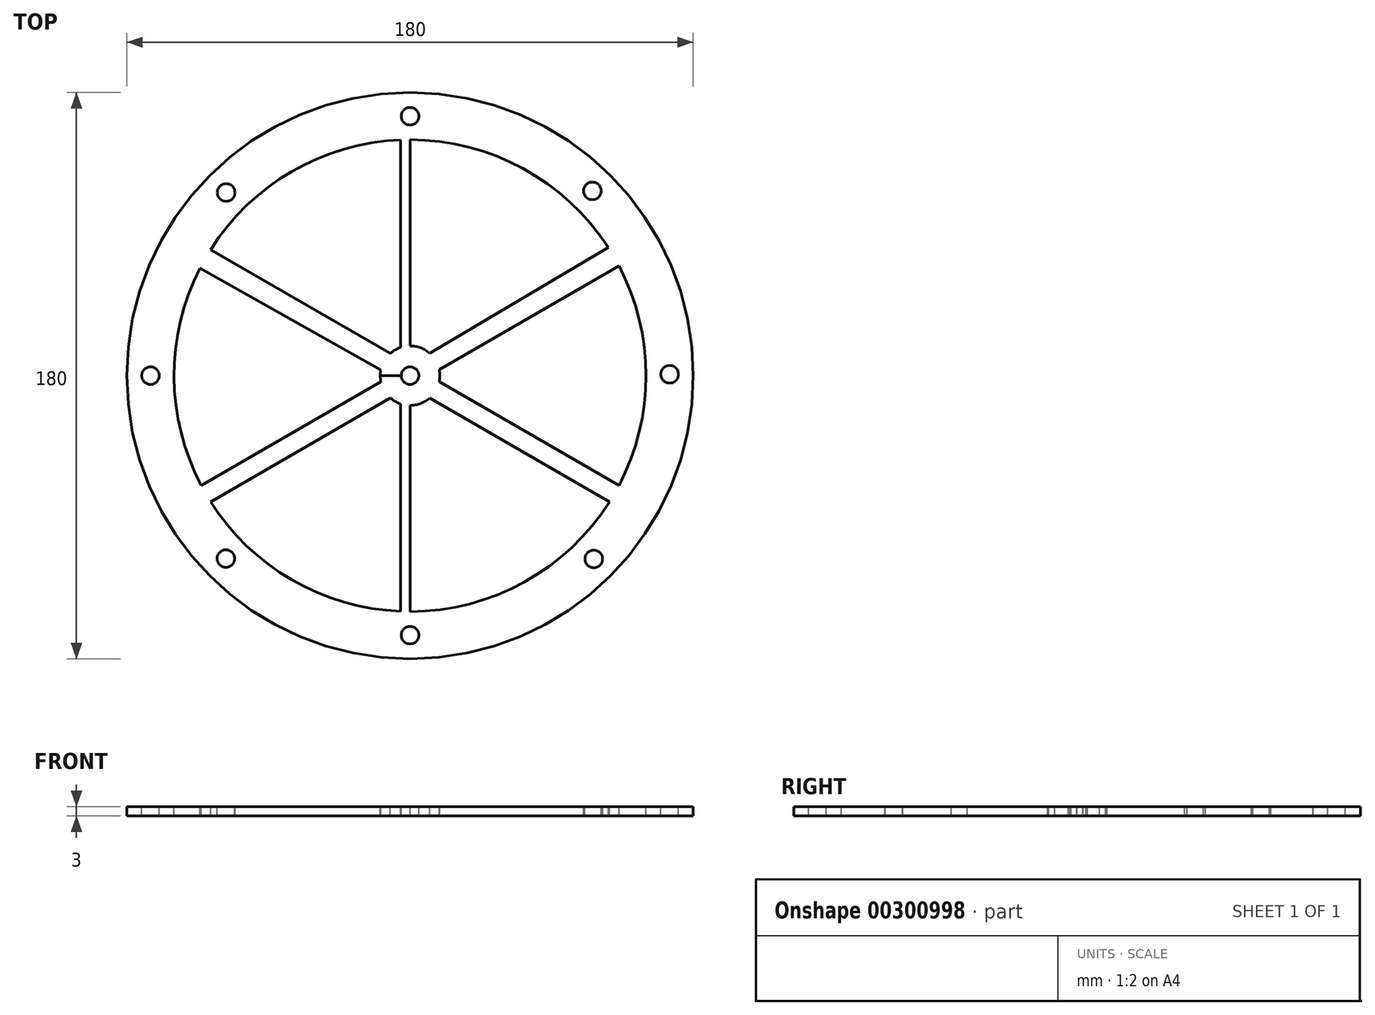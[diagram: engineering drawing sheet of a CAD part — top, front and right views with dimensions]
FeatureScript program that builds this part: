
annotation { "Feature Type Name" : "Feature", "Feature Type Description" : "" }
export const myFeature = defineFeature(function(context is Context, id is Id, definition is map)
    precondition{}
    {
        {
            var Q0;
            Q0=qCreatedBy(makeId("Top.planeOp"),FACE);
            var sketch = newSketch(context, id + "F0", { "sketchPlane" : qUnion([Q0])});
            skCircle(sketch, "E0", {"center": v(0, 0) * mm, "radius": 90 * mm});
            skCircle(sketch, "E1", {"center": v(0, 0) * mm, "radius": 75 * mm});
            skPoint(sketch, "E2", {"position": v(0, 82.48) * mm});
            skPoint(sketch, "E3", {"position": v(0, -82.5) * mm});
            skPoint(sketch, "E4", {"position": v(-75, 0) * mm});
            skPoint(sketch, "E5", {"position": v(-82.5, 0) * mm});
            skPoint(sketch, "E6", {"position": v(-58.44, 58.23) * mm});
            skPoint(sketch, "E7", {"position": v(82.5, 0.44) * mm});
            skPoint(sketch, "E8", {"position": v(57.94, 58.73) * mm});
            skPoint(sketch, "E9", {"position": v(-58.53, -58.15) * mm});
            skLineSegment(sketch, "E10", {"start": v(0, 0) * mm, "end": v(0, 0) * mm});
            skPoint(sketch, "E11", {"position": v(58.39, -58.28) * mm});
            skLineSegment(sketch, "E12", {"start": v(3, 74.94) * mm, "end": v(3, 8.6) * mm});
            skLineSegment(sketch, "E13", {"start": v(0, 75) * mm, "end": v(0, 0) * mm, "construction": true});
            skLineSegment(sketch, "E14", {"start": v(0, 75) * mm, "end": v(0, -75) * mm});
            skCircle(sketch, "E15", {"center": v(0, 0) * mm, "radius": 9.46 * mm});
            skLineSegment(sketch, "E16", {"start": v(0, 0) * mm, "end": v(82.5, 0.44) * mm});
            skLineSegment(sketch, "E17", {"start": v(-3, -8.98) * mm, "end": v(-3, -74.94) * mm});
            skLineSegment(sketch, "E18", {"start": v(0, 0) * mm, "end": v(-75, 0) * mm});
            skLineSegment(sketch, "E19", {"start": v(3, -74.88) * mm, "end": v(0, -75) * mm});
            skLineSegment(sketch, "E20", {"start": v(-3, 74.94) * mm, "end": v(-3, 8.97) * mm});
            skLineSegment(sketch, "E21.MirrorCS", {"start": v(0, 0) * mm, "end": v(-75, -0.8) * mm});
            skLineSegment(sketch, "E22.MirrorCS", {"start": v(3.8, -74.9) * mm, "end": v(3.1, -8.57) * mm});
            skLineSegment(sketch, "E23.1.0", {"start": v(62.97, 40.75) * mm, "end": v(5.88, 6.96) * mm});
            skLineSegment(sketch, "E23.2.0", {"start": v(-66.77, 34.16) * mm, "end": v(-8.97, 1.6) * mm});
            skLineSegment(sketch, "E24.1.0", {"start": v(9.27, 1.9) * mm, "end": v(66.4, 34.87) * mm});
            skLineSegment(sketch, "E24.1.1", {"start": v(-66.4, -34.87) * mm, "end": v(-8.95, -1.7) * mm});
            skLineSegment(sketch, "E24.2.0", {"start": v(-6.27, 7.09) * mm, "end": v(-63.4, 40.07) * mm});
            skLineSegment(sketch, "E24.2.1", {"start": v(63.4, -40.07) * mm, "end": v(5.95, -6.9) * mm});
            skLineSegment(sketch, "E25.1.0", {"start": v(-63.4, -40.07) * mm, "end": v(-6.27, -7.08) * mm});
            skLineSegment(sketch, "E25.2.0", {"start": v(66.4, -34.87) * mm, "end": v(9.27, -1.89) * mm});
            skCircle(sketch, "E26", {"center": v(0, 0) * mm, "radius": 2.8 * mm});
            skSolve(sketch);
        }
        {
            var Q0;
            Q0=makeQuery(id+"F0.imprint","IMPRINT",FACE,{"disambiguationData":[TD([[makeQuery(id+"F0.imprint","IMPRINT",EDGE,{"derivedFrom":sQuery(id+"F0.wireOp",EDGE,"E0")}),1.0]])]});
            var Q1;
            {var subQ1=sQuery(id+"F0.wireOp",EDGE,"E1");var subQ3=sQuery(id+"F0.wireOp",EDGE,"E14");var subQ4=makeQuery(id+"F0.imprint","INTERSECT",VERTEX,{"disambiguationData":[OD(0.0)],"derivedFrom":[subQ1,subQ3]});Q1=makeQuery(id+"F0.imprint","IMPRINT",FACE,{"disambiguationData":[TD([[makeQuery(id+"F0.imprint","IMPRINT",EDGE,{"disambiguationData":[TD([[subQ4,-1.0]])],"derivedFrom":subQ3}),1.0]])]});}
            var Q2;
            {var subQ0=sQuery(id+"F0.wireOp",EDGE,"E14");var subQ1=sQuery(id+"F0.wireOp",EDGE,"E1");var subQ2=makeQuery(id+"F0.imprint","INTERSECT",VERTEX,{"disambiguationData":[OD(0.0)],"derivedFrom":[subQ1,subQ0]});Q2=makeQuery(id+"F0.imprint","IMPRINT",FACE,{"disambiguationData":[TD([[makeQuery(id+"F0.imprint","IMPRINT",EDGE,{"disambiguationData":[TD([[subQ2,-1.0]])],"derivedFrom":subQ0}),-1.0]])]});}
            var Q3;
            {var subQ7=sQuery(id+"F0.wireOp",EDGE,"E24.2.0");Q3=makeQuery(id+"F0.imprint","IMPRINT",FACE,{"disambiguationData":[TD([[makeQuery(id+"F0.imprint","IMPRINT",EDGE,{"derivedFrom":subQ7}),1.0]])]});}
            var Q4;
            {var subQ3=sQuery(id+"F0.wireOp",EDGE,"E24.1.0");Q4=makeQuery(id+"F0.imprint","IMPRINT",FACE,{"disambiguationData":[TD([[makeQuery(id+"F0.imprint","IMPRINT",EDGE,{"derivedFrom":subQ3}),1.0]])]});}
            var Q5;
            {var subQ0=sQuery(id+"F0.wireOp",EDGE,"E24.2.1");var subQ1=sQuery(id+"F0.wireOp",EDGE,"E1");var subQ2=makeQuery(id+"F0.imprint","INTERSECT",VERTEX,{"derivedFrom":[subQ1,subQ0]});Q5=makeQuery(id+"F0.imprint","IMPRINT",FACE,{"disambiguationData":[TD([[makeQuery(id+"F0.imprint","IMPRINT",EDGE,{"disambiguationData":[TD([[subQ2,-1.0]])],"derivedFrom":subQ1}),1.0]])]});}
            var Q6;
            {var subQ3=sQuery(id+"F0.wireOp",EDGE,"E17");Q6=makeQuery(id+"F0.imprint","IMPRINT",FACE,{"disambiguationData":[TD([[makeQuery(id+"F0.imprint","IMPRINT",EDGE,{"derivedFrom":subQ3}),1.0]])]});}
            var Q7;
            {var subQ0=sQuery(id+"F0.wireOp",EDGE,"E14");var subQ1=sQuery(id+"F0.wireOp",EDGE,"E1");var subQ2=makeQuery(id+"F0.imprint","INTERSECT",VERTEX,{"disambiguationData":[OD(1.0)],"derivedFrom":[subQ1,subQ0]});Q7=makeQuery(id+"F0.imprint","IMPRINT",FACE,{"disambiguationData":[TD([[makeQuery(id+"F0.imprint","IMPRINT",EDGE,{"disambiguationData":[TD([[subQ2,-1.0]])],"derivedFrom":subQ1}),1.0]])]});}
            var Q8;
            {var subQ0=sQuery(id+"F0.wireOp",EDGE,"E24.1.1");var subQ1=sQuery(id+"F0.wireOp",EDGE,"E1");var subQ2=makeQuery(id+"F0.imprint","INTERSECT",VERTEX,{"derivedFrom":[subQ1,subQ0]});Q8=makeQuery(id+"F0.imprint","IMPRINT",FACE,{"disambiguationData":[TD([[makeQuery(id+"F0.imprint","IMPRINT",EDGE,{"disambiguationData":[TD([[subQ2,-1.0]])],"derivedFrom":subQ1}),1.0]])]});}
            var Q9;
            {var subQ0=sQuery(id+"F0.wireOp",EDGE,"E15");var subQ3=makeQuery(id+"F0.imprint","INTERSECT",VERTEX,{"derivedFrom":[subQ0,sQuery(id+"F0.wireOp",EDGE,"E24.1.1")]});Q9=makeQuery(id+"F0.imprint","IMPRINT",FACE,{"disambiguationData":[TD([[makeQuery(id+"F0.imprint","IMPRINT",EDGE,{"disambiguationData":[TD([[subQ3,1.0]])],"derivedFrom":subQ0}),1.0]])]});}
            var Q10;
            {var subQ0=sQuery(id+"F0.wireOp",EDGE,"E15");var subQ3=makeQuery(id+"F0.imprint","INTERSECT",VERTEX,{"derivedFrom":[subQ0,sQuery(id+"F0.wireOp",EDGE,"E20")]});Q10=makeQuery(id+"F0.imprint","IMPRINT",FACE,{"disambiguationData":[TD([[makeQuery(id+"F0.imprint","IMPRINT",EDGE,{"disambiguationData":[TD([[subQ3,1.0]])],"derivedFrom":subQ0}),1.0]])]});}
            var Q11;
            {var subQ0=sQuery(id+"F0.wireOp",EDGE,"E15");var subQ1=makeQuery(id+"F0.imprint","INTERSECT",VERTEX,{"derivedFrom":[subQ0,sQuery(id+"F0.wireOp",EDGE,"E24.1.0")]});Q11=makeQuery(id+"F0.imprint","IMPRINT",FACE,{"disambiguationData":[TD([[makeQuery(id+"F0.imprint","IMPRINT",EDGE,{"disambiguationData":[TD([[subQ1,1.0]])],"derivedFrom":subQ0}),1.0]])]});}
            var Q12;
            {var subQ0=sQuery(id+"F0.wireOp",EDGE,"E15");var subQ3=makeQuery(id+"F0.imprint","INTERSECT",VERTEX,{"derivedFrom":[subQ0,sQuery(id+"F0.wireOp",EDGE,"E22.MirrorCS")]});Q12=makeQuery(id+"F0.imprint","IMPRINT",FACE,{"disambiguationData":[TD([[makeQuery(id+"F0.imprint","IMPRINT",EDGE,{"disambiguationData":[TD([[subQ3,1.0]])],"derivedFrom":subQ0}),1.0]])]});}
            extrude(context, id + "F1", {"entities" : qUnion([Q0, Q1, Q2, Q3, Q4, Q5, Q6, Q7, Q8, Q9, Q10, Q11, Q12]), "oppositeDirection" : true, "offsetDistance" : 25 * mm, "depth" : 3 * mm});
        }
        {
            var Q0;
            Q0=sQuery(id+"F0.wireOp",VERTEX,"E5");
            var Q1;
            Q1=sQuery(id+"F0.wireOp",VERTEX,"E2");
            var Q2;
            Q2=sQuery(id+"F0.wireOp",VERTEX,"E6");
            var Q3;
            Q3=sQuery(id+"F0.wireOp",VERTEX,"E8");
            var Q4;
            Q4=sQuery(id+"F0.wireOp",VERTEX,"E7");
            var Q5;
            Q5=sQuery(id+"F0.wireOp",VERTEX,"E11");
            var Q6;
            Q6=sQuery(id+"F0.wireOp",VERTEX,"E3");
            var Q7;
            Q7=sQuery(id+"F0.wireOp",VERTEX,"E9");
            var Q8;
            Q8=makeQuery(id+"F1.opExtrude","SWEPT_BODY",BODY,{"disambiguationData":[OSD([sQuery(id+"F0.wireOp",EDGE,"E0"),sQuery(id+"F0.wireOp",EDGE,"E1")])]});
            hole(context, id + "F2", {"style" : HoleStyle.SIMPLE, "endStyle" : HoleEndStyle.BLIND, "holeDiameter" : 5.6 * mm, "holeDepth" : 3 * mm, "isTappedThrough" : true, "tappedDepth" : 12 * mm, "tapClearance" : 3, "locations" : qUnion([Q0, Q1, Q2, Q3, Q4, Q5, Q6, Q7]), "scope" : qUnion([Q8]), "majorDiameter" : 5 * mm});
        }
    });
